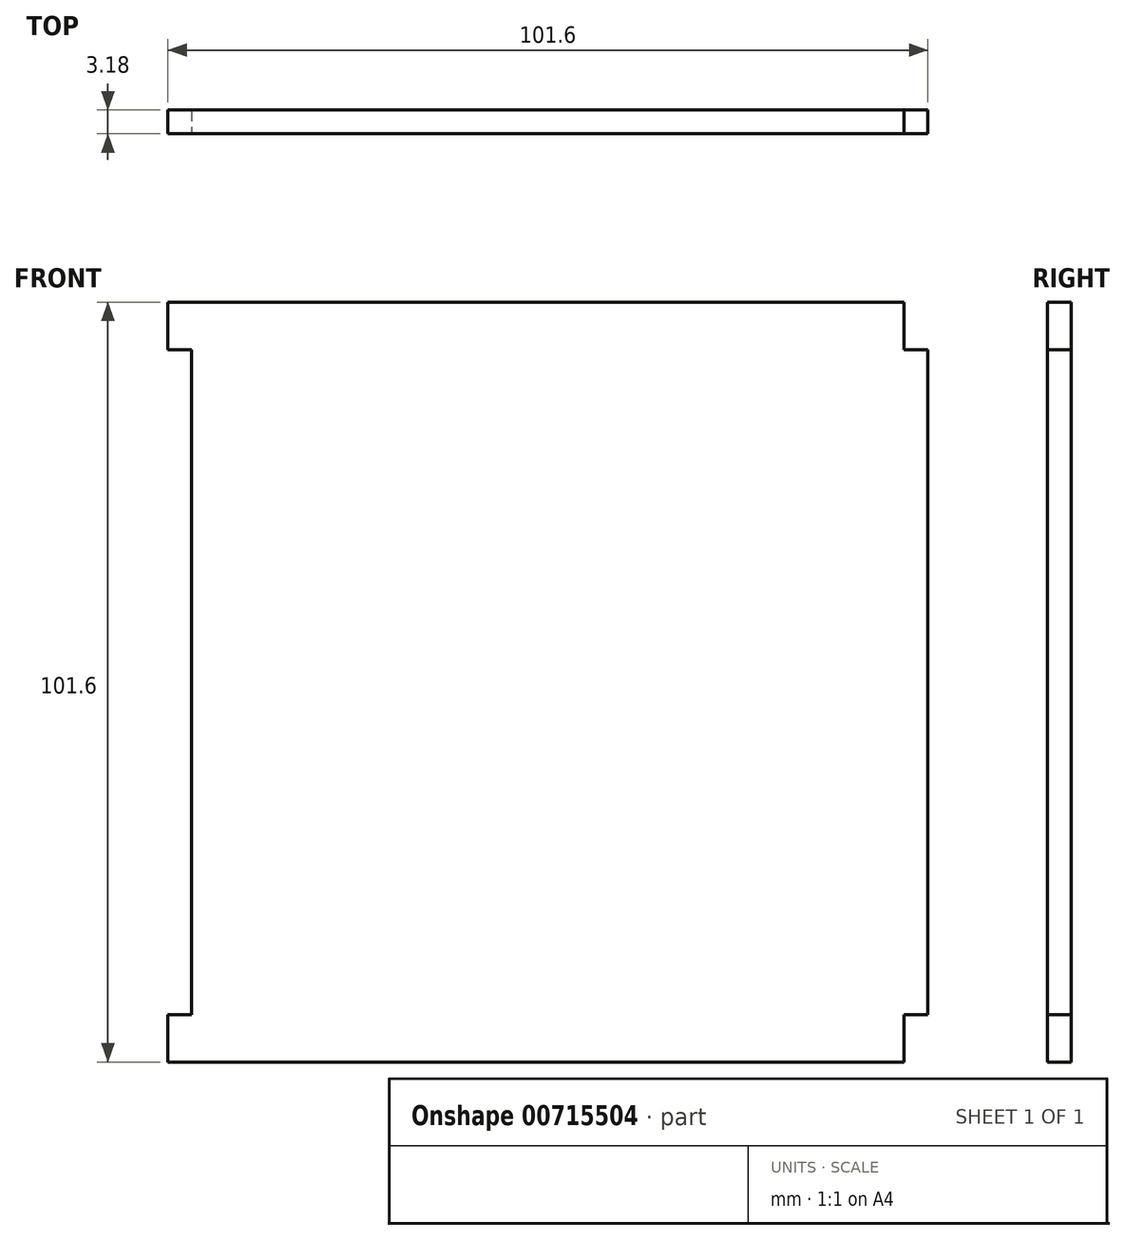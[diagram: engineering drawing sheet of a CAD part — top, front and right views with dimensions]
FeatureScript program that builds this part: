
annotation { "Feature Type Name" : "Feature", "Feature Type Description" : "" }
export const myFeature = defineFeature(function(context is Context, id is Id, definition is map)
    precondition{}
    {
        {
            var Q0;
            Q0=qCreatedBy(makeId("Front.planeOp"),FACE);
            var sketch = newSketch(context, id + "F0", { "sketchPlane" : qUnion([Q0])});
            skLineSegment(sketch, "E0.bottom", {"start": v(50.8, -50.8) * mm, "end": v(-50.8, -50.8) * mm});
            skLineSegment(sketch, "E0.top", {"start": v(50.8, 50.8) * mm, "end": v(-50.8, 50.8) * mm});
            skLineSegment(sketch, "E0.left", {"start": v(50.8, -50.8) * mm, "end": v(50.8, 50.8) * mm});
            skLineSegment(sketch, "E0.right", {"start": v(-50.8, -50.8) * mm, "end": v(-50.8, 50.8) * mm});
            skPoint(sketch, "E0.middle", {"position": v(0, 0) * mm});
            skSolve(sketch);
        }
        {
            var Q0;
            Q0=makeQuery(id+"F0.imprint","IMPRINT",FACE,{"disambiguationData":[TD([[makeQuery(id+"F0.imprint","IMPRINT",EDGE,{"derivedFrom":sQuery(id+"F0.wireOp",EDGE,"E0.bottom")}),-1.0]])]});
            extrude(context, id + "F1", {"entities" : qUnion([Q0]), "depth" : 3.17 * mm, "offsetDistance" : 25.4 * mm});
        }
        {
            var Q0;
            Q0=makeQuery(id+"F1.opExtrude","CAP_FACE",FACE,{"disambiguationData":[OSD([sQuery(id+"F0.wireOp",EDGE,"E0.bottom"),sQuery(id+"F0.wireOp",EDGE,"E0.top"),sQuery(id+"F0.wireOp",EDGE,"E0.left"),sQuery(id+"F0.wireOp",EDGE,"E0.right")])],"isStart":false});
            var sketch = newSketch(context, id + "F2", { "sketchPlane" : qUnion([Q0])});
            skLineSegment(sketch, "E1.bottom", {"start": v(50.8, 50.8) * mm, "end": v(47.63, 50.8) * mm});
            skLineSegment(sketch, "E1.top", {"start": v(50.8, 44.45) * mm, "end": v(47.63, 44.45) * mm});
            skLineSegment(sketch, "E1.left", {"start": v(50.8, 50.8) * mm, "end": v(50.8, 44.45) * mm});
            skLineSegment(sketch, "E1.right", {"start": v(47.63, 50.8) * mm, "end": v(47.63, 44.45) * mm});
            skLineSegment(sketch, "E2.bottom", {"start": v(50.8, -50.8) * mm, "end": v(47.63, -50.8) * mm});
            skLineSegment(sketch, "E2.top", {"start": v(50.8, -44.45) * mm, "end": v(47.63, -44.45) * mm});
            skLineSegment(sketch, "E2.left", {"start": v(50.8, -50.8) * mm, "end": v(50.8, -44.45) * mm});
            skLineSegment(sketch, "E2.right", {"start": v(47.63, -50.8) * mm, "end": v(47.63, -44.45) * mm});
            skLineSegment(sketch, "E3", {"start": v(-50.8, 50.8) * mm, "end": v(-50.8, 44.45) * mm});
            skLineSegment(sketch, "E4.bottom", {"start": v(-50.8, 44.45) * mm, "end": v(-47.63, 44.45) * mm});
            skLineSegment(sketch, "E4.top", {"start": v(-50.8, -44.45) * mm, "end": v(-47.63, -44.45) * mm});
            skLineSegment(sketch, "E4.left", {"start": v(-50.8, 44.45) * mm, "end": v(-50.8, -44.45) * mm});
            skLineSegment(sketch, "E4.right", {"start": v(-47.63, 44.45) * mm, "end": v(-47.63, -44.45) * mm});
            skSolve(sketch);
        }
        {
            var Q0;
            Q0=makeQuery(id+"F2.imprint","IMPRINT",FACE,{"disambiguationData":[TD([[makeQuery(id+"F2.imprint","IMPRINT",EDGE,{"derivedFrom":sQuery(id+"F2.wireOp",EDGE,"E4.bottom")}),-1.0]])]});
            var Q1;
            Q1=makeQuery(id+"F2.imprint","IMPRINT",FACE,{"disambiguationData":[TD([[makeQuery(id+"F2.imprint","IMPRINT",EDGE,{"derivedFrom":sQuery(id+"F2.wireOp",EDGE,"E1.bottom")}),1.0]])]});
            var Q2;
            Q2=makeQuery(id+"F2.imprint","IMPRINT",FACE,{"disambiguationData":[TD([[makeQuery(id+"F2.imprint","IMPRINT",EDGE,{"derivedFrom":sQuery(id+"F2.wireOp",EDGE,"E2.bottom")}),-1.0]])]});
            extrude(context, id + "F3", {"entities" : qUnion([Q0, Q1, Q2]), "operationType" : NewBodyOperationType.REMOVE, "oppositeDirection" : true, "depth" : 25.4 * mm, "offsetDistance" : 25.4 * mm});
        }
    });
